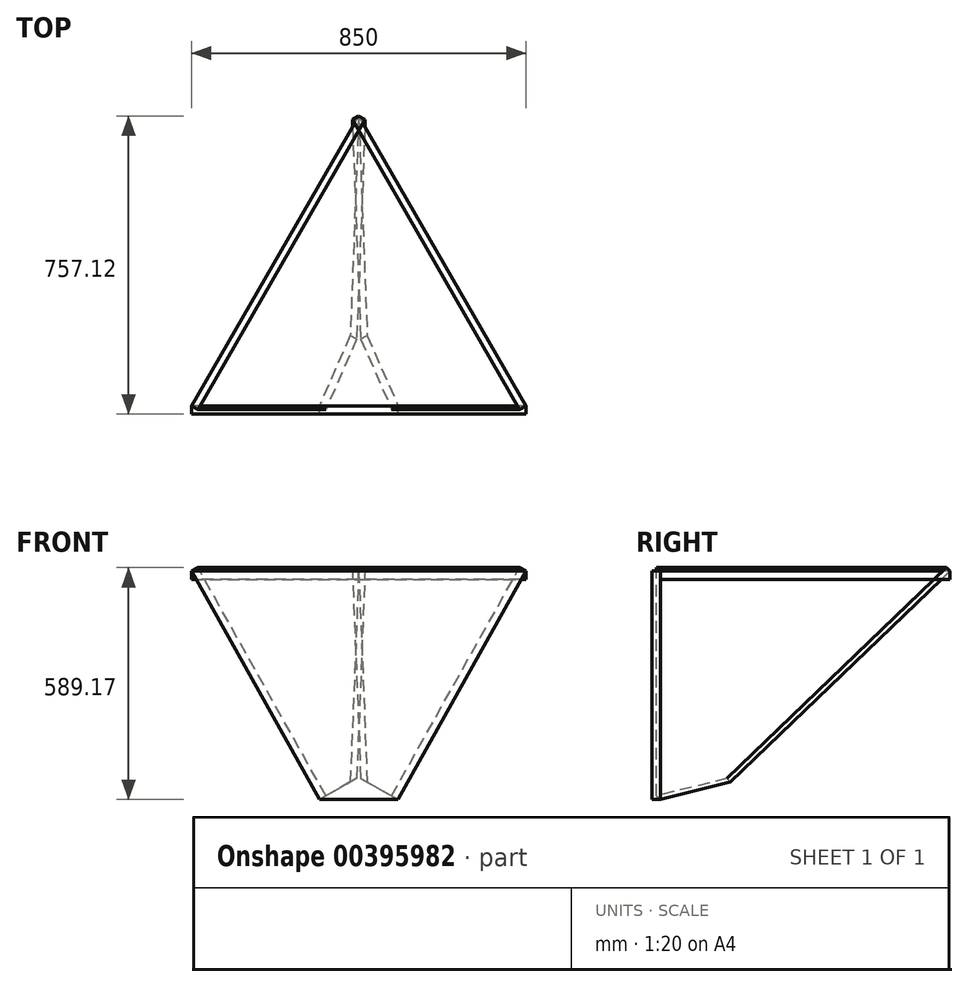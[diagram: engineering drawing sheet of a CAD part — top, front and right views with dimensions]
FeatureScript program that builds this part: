
annotation { "Feature Type Name" : "Feature", "Feature Type Description" : "" }
export const myFeature = defineFeature(function(context is Context, id is Id, definition is map)
    precondition{}
    {
        {
            var Q0;
            Q0=qCreatedBy(makeId("Front.planeOp"),FACE);
            var sketch = newSketch(context, id + "F0", { "sketchPlane" : qUnion([Q0])});
            skLineSegment(sketch, "E0", {"start": v(-425, 580) * mm, "end": v(-100, 0) * mm});
            skLineSegment(sketch, "E1", {"start": v(-100, 0) * mm, "end": v(100, 0) * mm});
            skLineSegment(sketch, "E2", {"start": v(100, 0) * mm, "end": v(425, 580) * mm});
            skLineSegment(sketch, "E3", {"start": v(425, 580) * mm, "end": v(-425, 580) * mm});
            skSolve(sketch);
        }
        {
            var Q0;
            Q0=makeQuery(id+"F0.imprint","IMPRINT",FACE,{"disambiguationData":[TD([[makeQuery(id+"F0.imprint","IMPRINT",EDGE,{"derivedFrom":sQuery(id+"F0.wireOp",EDGE,"E0")}),1.0]])]});
            extrude(context, id + "F1", {"entities" : qUnion([Q0]), "depth" : 21 * mm});
        }
        {
            var Q0;
            Q0=makeQuery(id+"F1.opExtrude","SWEPT_FACE",FACE,{"disambiguationData":[OSD([sQuery(id+"F0.wireOp",EDGE,"E3")])]});
            var sketch = newSketch(context, id + "F2", { "sketchPlane" : qUnion([Q0])});
            skLineSegment(sketch, "E4", {"start": v(-425, 0) * mm, "end": v(0, 736.12) * mm});
            skLineSegment(sketch, "E5", {"start": v(0, 736.12) * mm, "end": v(425, 0) * mm});
            skSolve(sketch);
        }
        {
            var Q0;
            Q0 = qSketchRegion(id + "F2", true);
            var Q1;
            Q1=makeQuery(id+"F2.imprint","IMPRINT",FACE,{"disambiguationData":[TD([[makeQuery(id+"F2.imprint","IMPRINT",EDGE,{"derivedFrom":sQuery(id+"F2.wireOp",EDGE,"E4")}),-1.0]])]});
            extrude(context, id + "F3", {"entities" : qUnion([Q0, Q1]), "oppositeDirection" : true, "depth" : 21 * mm});
        }
        {
            var Q0;
            Q0=makeQuery(id+"F1.opExtrude","CAP_VERTEX",VERTEX,{"disambiguationData":[OSD([sQuery(id+"F0.wireOp",EDGE,"E2"),sQuery(id+"F0.wireOp",EDGE,"E3")])],"isStart":true});
            var Q1;
            Q1=makeQuery(id+"F1.opExtrude","CAP_VERTEX",VERTEX,{"disambiguationData":[OSD([sQuery(id+"F0.wireOp",EDGE,"E1"),sQuery(id+"F0.wireOp",EDGE,"E2")])],"isStart":true});
            var Q2;
            Q2=makeQuery(id+"F3.opExtrude","CAP_VERTEX",VERTEX,{"disambiguationData":[OSD([sQuery(id+"F2.wireOp",EDGE,"E4"),sQuery(id+"F2.wireOp",EDGE,"E5")])],"isStart":true});
            cPlane(context, id + "F4", {"entities" : qUnion([Q0, Q1, Q2]), "cplaneType" : CPlaneType.THREE_POINT, "offset" : 25 * mm, "width" : 150 * mm, "height" : 150 * mm});
        }
        {
            var Q0;
            Q0=qCreatedBy(id+"F4.planeOp",FACE);
            var sketch = newSketch(context, id + "F5", { "sketchPlane" : qUnion([Q0])});
            skLineSegment(sketch, "E6", {"start": v(39.24, 713.73) * mm, "end": v(-784.98, 505.98) * mm});
            skLineSegment(sketch, "E7", {"start": v(-784.98, 505.98) * mm, "end": v(-160.76, 48.88) * mm});
            skLineSegment(sketch, "E8", {"start": v(-160.76, 48.88) * mm, "end": v(39.24, 48.88) * mm});
            skLineSegment(sketch, "E9", {"start": v(39.24, 48.88) * mm, "end": v(39.24, 713.73) * mm});
            skSolve(sketch);
        }
        {
            var Q0;
            Q0 = qSketchRegion(id + "F5", true);
            extrude(context, id + "F6", {"entities" : qUnion([Q0]), "depth" : 21 * mm});
        }
        {
            var Q0;
            Q0=makeQuery(id+"F6.opExtrude","SWEPT_BODY",BODY,{"disambiguationData":[OSD([sQuery(id+"F5.wireOp",EDGE,"E6"),sQuery(id+"F5.wireOp",EDGE,"E7"),sQuery(id+"F5.wireOp",EDGE,"E8"),sQuery(id+"F5.wireOp",EDGE,"E9")])]});
            var Q1;
            Q1=qCreatedBy(makeId("Right.planeOp"),FACE);
            mirror(context, id + "F7", {"entities" : qUnion([Q0]), "mirrorPlane" : qUnion([Q1])});
        }
    });
